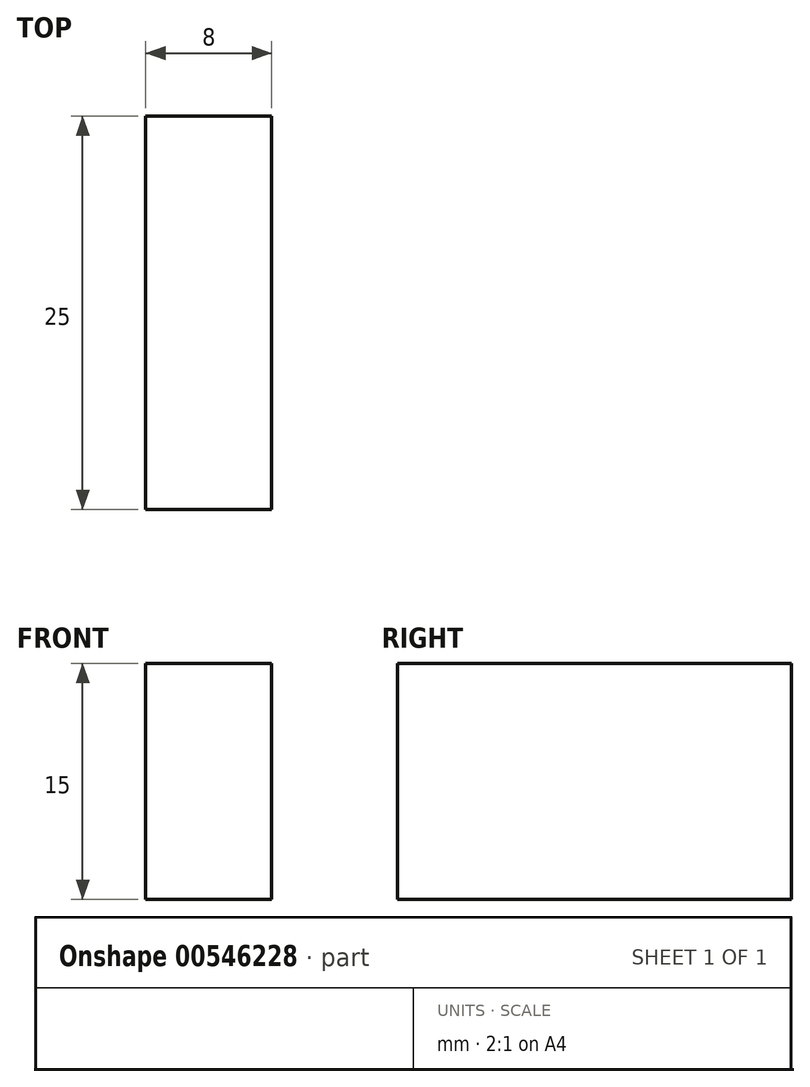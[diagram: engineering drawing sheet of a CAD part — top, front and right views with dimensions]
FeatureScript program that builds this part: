
annotation { "Feature Type Name" : "Feature", "Feature Type Description" : "" }
export const myFeature = defineFeature(function(context is Context, id is Id, definition is map)
    precondition{}
    {
        {
            var Q0;
            Q0=qCreatedBy(makeId("Right.planeOp"),FACE);
            var sketch = newSketch(context, id + "F0", { "sketchPlane" : qUnion([Q0])});
            skLineSegment(sketch, "E0.bottom", {"start": v(12.5, 7.5) * mm, "end": v(-12.5, 7.5) * mm});
            skLineSegment(sketch, "E0.top", {"start": v(12.5, -7.5) * mm, "end": v(-12.5, -7.5) * mm});
            skLineSegment(sketch, "E0.left", {"start": v(12.5, 7.5) * mm, "end": v(12.5, -7.5) * mm});
            skLineSegment(sketch, "E0.right", {"start": v(-12.5, 7.5) * mm, "end": v(-12.5, -7.5) * mm});
            skPoint(sketch, "E0.middle", {"position": v(0, 0) * mm});
            skSolve(sketch);
        }
        {
            var Q0;
            Q0=makeQuery(id+"F0.imprint","IMPRINT",FACE,{"disambiguationData":[TD([[makeQuery(id+"F0.imprint","IMPRINT",EDGE,{"derivedFrom":sQuery(id+"F0.wireOp",EDGE,"E0.bottom")}),1.0]])]});
            extrude(context, id + "F1", {"entities" : qUnion([Q0]), "depth" : 8 * mm, "offsetDistance" : 25 * mm});
        }
    });
